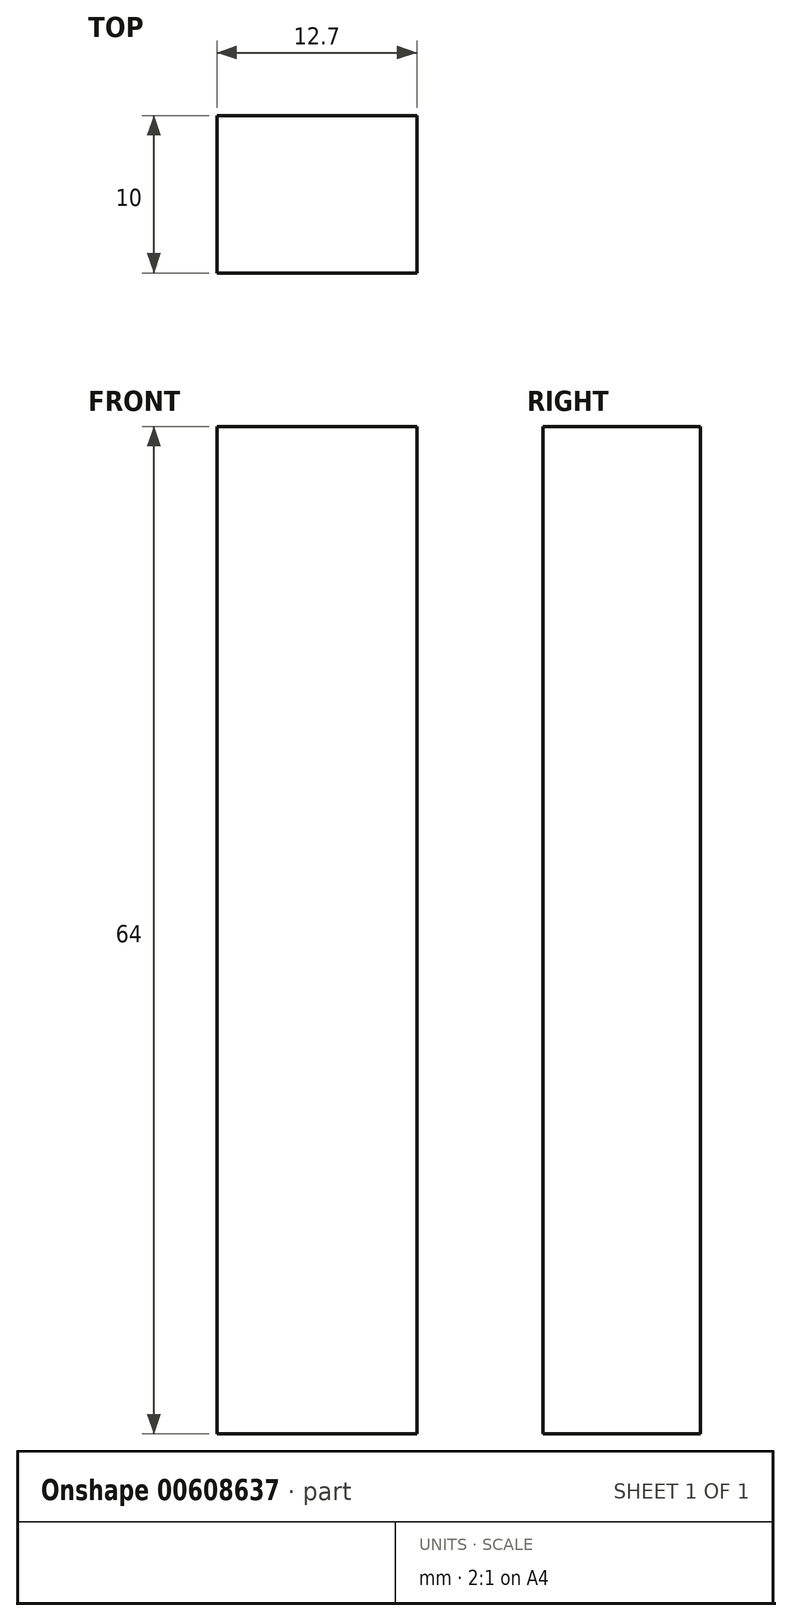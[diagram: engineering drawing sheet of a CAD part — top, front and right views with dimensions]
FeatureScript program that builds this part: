
annotation { "Feature Type Name" : "Feature", "Feature Type Description" : "" }
export const myFeature = defineFeature(function(context is Context, id is Id, definition is map)
    precondition{}
    {
        {
            var Q0;
            Q0=qCreatedBy(makeId("Front.planeOp"),FACE);
            var sketch = newSketch(context, id + "F0", { "sketchPlane" : qUnion([Q0])});
            skLineSegment(sketch, "E0.bottom", {"start": v(-6.35, 32) * mm, "end": v(6.35, 32) * mm});
            skLineSegment(sketch, "E0.top", {"start": v(-6.35, -32) * mm, "end": v(6.35, -32) * mm});
            skLineSegment(sketch, "E0.left", {"start": v(-6.35, 32) * mm, "end": v(-6.35, -32) * mm});
            skLineSegment(sketch, "E0.right", {"start": v(6.35, 32) * mm, "end": v(6.35, -32) * mm});
            skSolve(sketch);
        }
        {
            var Q0;
            Q0 = qSketchRegion(id + "F0", true);
            extrude(context, id + "F1", {"entities" : qUnion([Q0]), "endBound" : BoundingType.SYMMETRIC, "depth" : 10 * mm, "offsetDistance" : 25 * mm});
        }
    });
